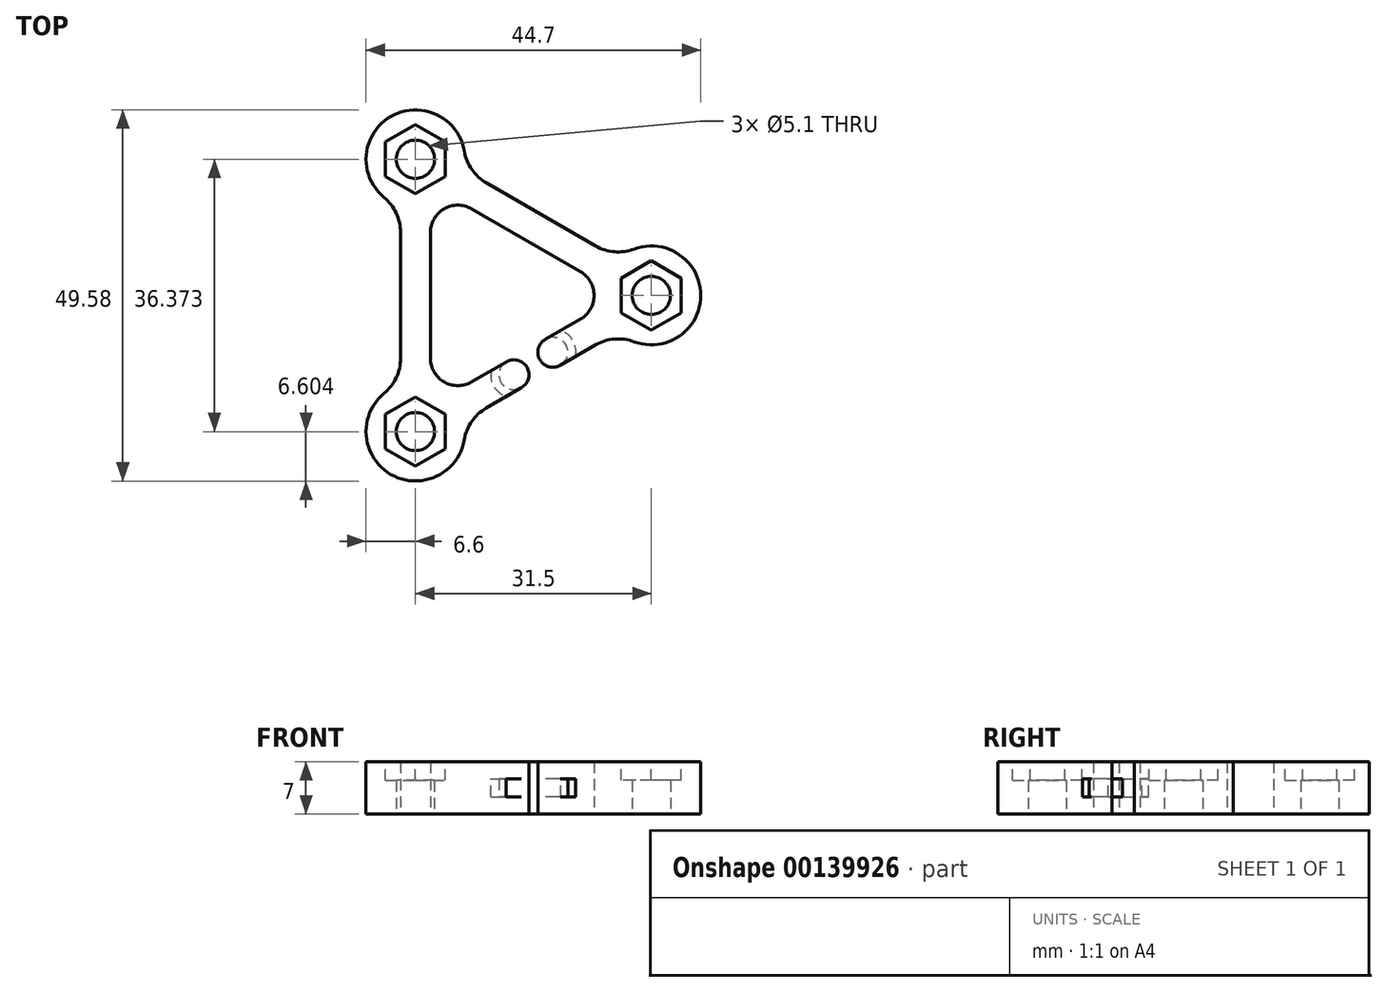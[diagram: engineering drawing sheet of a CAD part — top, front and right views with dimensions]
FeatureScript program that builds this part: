
annotation { "Feature Type Name" : "Feature", "Feature Type Description" : "" }
export const myFeature = defineFeature(function(context is Context, id is Id, definition is map)
    precondition{}
    {
        {
            var Q0;
            Q0=qCreatedBy(makeId("Top.planeOp"),FACE);
            var sketch = newSketch(context, id + "F0", { "sketchPlane" : qUnion([Q0])});
            skCircle(sketch, "E0", {"center": v(-31.5, 18.19) * mm, "radius": 2.55 * mm});
            skCircle(sketch, "E1", {"center": v(-31.5, -18.19) * mm, "radius": 2.55 * mm});
            skCircle(sketch, "E2", {"center": v(0, 0) * mm, "radius": 2.55 * mm});
            skArc(sketch, "E3", {"start": v(-25, 19.3) * mm, "mid": v(-34.8, 23.9) * mm, "end": v(-35.7, 13.1) * mm});
            skArc(sketch, "E4", {"start": v(-35.7, -13.1) * mm, "mid": v(-34.8, -23.9) * mm, "end": v(-25, -19.3) * mm});
            skArc(sketch, "E5", {"start": v(-2.3, -6.19) * mm, "mid": v(6.6, 0) * mm, "end": v(-2.3, 6.19) * mm});
            skLineSegment(sketch, "E6", {"start": v(-24.03, 11.56) * mm, "end": v(-9.47, 3.16) * mm});
            skLineSegment(sketch, "E7", {"start": v(-22.03, 15.03) * mm, "end": v(-7.47, 6.62) * mm});
            skLineSegment(sketch, "E8", {"start": v(-31.5, 18.19) * mm, "end": v(0, 0) * mm, "construction": true});
            skLineSegment(sketch, "E9", {"start": v(0, 0) * mm, "end": v(-31.5, -18.19) * mm, "construction": true});
            skLineSegment(sketch, "E10", {"start": v(-31.5, -18.19) * mm, "end": v(-31.5, 18.19) * mm, "construction": true});
            skArc(sketch, "E11", {"start": v(-24.03, 11.56) * mm, "mid": v(-27.68, 11.56) * mm, "end": v(-29.5, 8.4) * mm});
            skArc(sketch, "E12", {"start": v(-29.5, -8.4) * mm, "mid": v(-27.68, -11.56) * mm, "end": v(-24.03, -11.56) * mm});
            skArc(sketch, "E13", {"start": v(-9.47, -3.16) * mm, "mid": v(-7.65, 0) * mm, "end": v(-9.47, 3.16) * mm});
            skArc(sketch, "E14", {"start": v(-35.7, -13.1) * mm, "mid": v(-34.08, -11) * mm, "end": v(-33.5, -8.4) * mm});
            skArc(sketch, "E15", {"start": v(-22.03, -15.03) * mm, "mid": v(-23.99, -16.83) * mm, "end": v(-25, -19.3) * mm});
            skArc(sketch, "E16", {"start": v(-33.5, 8.4) * mm, "mid": v(-34.08, 11) * mm, "end": v(-35.7, 13.1) * mm});
            skArc(sketch, "E17", {"start": v(-25, 19.3) * mm, "mid": v(-23.99, 16.83) * mm, "end": v(-22.03, 15.03) * mm});
            skArc(sketch, "E18", {"start": v(-7.47, 6.62) * mm, "mid": v(-4.93, 5.83) * mm, "end": v(-2.3, 6.19) * mm});
            skArc(sketch, "E19", {"start": v(-2.3, -6.19) * mm, "mid": v(-4.93, -5.83) * mm, "end": v(-7.47, -6.62) * mm});
            skLineSegment(sketch, "E20", {"start": v(-24.03, 11.56) * mm, "end": v(-22.03, 15.03) * mm, "construction": true});
            skLineSegment(sketch, "E21", {"start": v(-9.47, 3.16) * mm, "end": v(-7.47, 6.62) * mm, "construction": true});
            skLineSegment(sketch, "E22", {"start": v(-9.47, -3.16) * mm, "end": v(-7.47, -6.62) * mm, "construction": true});
            skLineSegment(sketch, "E23", {"start": v(-33.5, -8.4) * mm, "end": v(-29.5, -8.4) * mm, "construction": true});
            skLineSegment(sketch, "E24", {"start": v(-22.03, -15.03) * mm, "end": v(-24.03, -11.56) * mm, "construction": true});
            skLineSegment(sketch, "E25", {"start": v(-33.5, -8.4) * mm, "end": v(-33.5, 8.4) * mm});
            skLineSegment(sketch, "E26", {"start": v(-29.5, -8.4) * mm, "end": v(-29.5, 8.4) * mm});
            skLineSegment(sketch, "E27", {"start": v(-33.5, 8.4) * mm, "end": v(-29.5, 8.4) * mm, "construction": true});
            skLineSegment(sketch, "E28", {"start": v(-24.03, -11.56) * mm, "end": v(-19.35, -8.86) * mm});
            skLineSegment(sketch, "E29", {"start": v(-14.15, -5.86) * mm, "end": v(-9.47, -3.16) * mm});
            skLineSegment(sketch, "E30", {"start": v(-22.03, -15.03) * mm, "end": v(-17.35, -12.33) * mm});
            skLineSegment(sketch, "E31", {"start": v(-7.47, -6.62) * mm, "end": v(-12.15, -9.33) * mm});
            skArc(sketch, "E32", {"start": v(-17.35, -12.33) * mm, "mid": v(-16.62, -9.6) * mm, "end": v(-19.35, -8.86) * mm});
            skArc(sketch, "E33", {"start": v(-14.15, -5.86) * mm, "mid": v(-14.88, -8.6) * mm, "end": v(-12.15, -9.33) * mm});
            skSolve(sketch);
        }
        {
            var Q0;
            Q0=makeQuery(id+"F0.imprint","IMPRINT",FACE,{"disambiguationData":[TD([[makeQuery(id+"F0.imprint","IMPRINT",EDGE,{"derivedFrom":sQuery(id+"F0.wireOp",EDGE,"E0")}),-1.0]])]});
            extrude(context, id + "F1", {"entities" : qUnion([Q0]), "depth" : 7 * mm});
        }
        {
            var Q0;
            Q0=makeQuery(id+"F1.opExtrude","CAP_FACE",FACE,{"disambiguationData":[OSD([sQuery(id+"F0.wireOp",EDGE,"E0"),sQuery(id+"F0.wireOp",EDGE,"E1"),sQuery(id+"F0.wireOp",EDGE,"E2"),sQuery(id+"F0.wireOp",EDGE,"E3"),sQuery(id+"F0.wireOp",EDGE,"E4"),sQuery(id+"F0.wireOp",EDGE,"E5"),sQuery(id+"F0.wireOp",EDGE,"T5Vw66OG-G5OR-DHDx-KvU7-dnTMRq0o1A0g"),sQuery(id+"F0.wireOp",EDGE,"8mzCXc7P-Lu7A-tcA2-hDls-zUZMRrlwUirj"),sQuery(id+"F0.wireOp",EDGE,"n4Ubmgs8-MzYA-ilAs-um63-DOsCIZ42xYd5"),sQuery(id+"F0.wireOp",EDGE,"iCspHw3C-Pdpp-QPBW-yDHl-MGOv44Ga2VXa"),sQuery(id+"F0.wireOp",EDGE,"xnWTmErK-ZSIG-ryMW-Ekzr-RR3PqCajZfuL"),sQuery(id+"F0.wireOp",EDGE,"AKW5OVUo-PFRE-jSi0-v7oE-Iw4JobIG5vWv"),sQuery(id+"F0.wireOp",EDGE,"E6"),sQuery(id+"F0.wireOp",EDGE,"JkiSf5jC-OJZR-1wmq-AVkU-QwjWYPwXVpW3"),sQuery(id+"F0.wireOp",EDGE,"9YlTFYq7-sXvY-dmJ4-6YRE-gBgDyT6P94yA")])],"isStart":false});
            var sketch = newSketch(context, id + "F2", { "sketchPlane" : qUnion([Q0])});
            skCircle(sketch, "E34.cCircle", {"center": v(-31.5, 18.19) * mm, "radius": 4 * mm, "construction": true});
            skLineSegment(sketch, "E34.0", {"start": v(-27.5, 20.5) * mm, "end": v(-27.5, 15.88) * mm});
            skLineSegment(sketch, "E34.1", {"start": v(-27.5, 15.88) * mm, "end": v(-31.5, 13.57) * mm});
            skLineSegment(sketch, "E34.2", {"start": v(-31.5, 13.57) * mm, "end": v(-35.5, 15.88) * mm});
            skLineSegment(sketch, "E34.3", {"start": v(-35.5, 15.88) * mm, "end": v(-35.5, 20.5) * mm});
            skLineSegment(sketch, "E34.4", {"start": v(-35.5, 20.5) * mm, "end": v(-31.5, 22.8) * mm});
            skLineSegment(sketch, "E34.5", {"start": v(-31.5, 22.8) * mm, "end": v(-27.5, 20.5) * mm});
            skPoint(sketch, "E34.0.midPoint", {"position": v(-27.5, 18.19) * mm});
            skCircle(sketch, "E35.cCircle", {"center": v(-31.5, -18.19) * mm, "radius": 4 * mm, "construction": true});
            skLineSegment(sketch, "E35.0", {"start": v(-27.5, -15.88) * mm, "end": v(-27.5, -20.5) * mm});
            skLineSegment(sketch, "E35.1", {"start": v(-27.5, -20.5) * mm, "end": v(-31.5, -22.8) * mm});
            skLineSegment(sketch, "E35.2", {"start": v(-31.5, -22.8) * mm, "end": v(-35.5, -20.5) * mm});
            skLineSegment(sketch, "E35.3", {"start": v(-35.5, -20.5) * mm, "end": v(-35.5, -15.88) * mm});
            skLineSegment(sketch, "E35.4", {"start": v(-35.5, -15.88) * mm, "end": v(-31.5, -13.57) * mm});
            skLineSegment(sketch, "E35.5", {"start": v(-31.5, -13.57) * mm, "end": v(-27.5, -15.88) * mm});
            skPoint(sketch, "E35.0.midPoint", {"position": v(-27.5, -18.19) * mm});
            skCircle(sketch, "E36.cCircle", {"center": v(0, 0) * mm, "radius": 4 * mm, "construction": true});
            skLineSegment(sketch, "E36.0", {"start": v(-4, -2.3) * mm, "end": v(-4, 2.3) * mm});
            skLineSegment(sketch, "E36.1", {"start": v(-4, 2.3) * mm, "end": v(0, 4.62) * mm});
            skLineSegment(sketch, "E36.2", {"start": v(0, 4.62) * mm, "end": v(4, 2.3) * mm});
            skLineSegment(sketch, "E36.3", {"start": v(4, 2.3) * mm, "end": v(4, -2.3) * mm});
            skLineSegment(sketch, "E36.4", {"start": v(4, -2.3) * mm, "end": v(0, -4.62) * mm});
            skLineSegment(sketch, "E36.5", {"start": v(0, -4.62) * mm, "end": v(-4, -2.3) * mm});
            skPoint(sketch, "E36.0.midPoint", {"position": v(-4, 0) * mm});
            skLineSegment(sketch, "E37", {"start": v(-31.5, -18.19) * mm, "end": v(-21, 0) * mm, "construction": true});
            skLineSegment(sketch, "E38", {"start": v(-21, 0) * mm, "end": v(-31.5, 18.19) * mm, "construction": true});
            skLineSegment(sketch, "E39", {"start": v(-21, 0) * mm, "end": v(0, 0) * mm, "construction": true});
            skLineSegment(sketch, "E40", {"start": v(-29, 0) * mm, "end": v(-17, 6.93) * mm, "construction": true});
            skPoint(sketch, "E40.startSnap0", {"position": v(-10.5, 0) * mm});
            skLineSegment(sketch, "E41", {"start": v(-17, 6.93) * mm, "end": v(-17, -6.93) * mm, "construction": true});
            skLineSegment(sketch, "E42", {"start": v(-17, -6.93) * mm, "end": v(-29, 0) * mm, "construction": true});
            skPoint(sketch, "E43", {"position": v(-23, 3.46) * mm});
            skPoint(sketch, "E44", {"position": v(-23, -3.46) * mm});
            skPoint(sketch, "E45", {"position": v(-17, 0) * mm});
            skSolve(sketch);
        }
        {
            var Q0;
            Q0=qSketchRegion(id+"F2",true);
            extrude(context, id + "F3", {"entities" : qUnion([Q0]), "operationType" : NewBodyOperationType.REMOVE, "oppositeDirection" : true, "depth" : 2.5 * mm});
        }
        {
            var Q0;
            Q0=qCreatedBy(makeId("Top.planeOp"),FACE);
            var Q1;
            Q1=makeQuery(id+"F2.imprint","IMPRINT",FACE,{"disambiguationData":[TD([[makeQuery(id+"F2.imprint","IMPRINT",EDGE,{"derivedFrom":sQuery(id+"F2.wireOp",EDGE,"E34.0")}),1.0]])]});
            cPlane(context, id + "F4", {"entities" : qUnion([Q0, Q1]), "cplaneType" : CPlaneType.MID_PLANE, "offset" : 3 * mm, "oppositeDirection" : true, "width" : 150 * mm, "height" : 150 * mm});
        }
        {
            var Q0;
            Q0=qCreatedBy(id+"F4.planeOp",FACE);
            var sketch = newSketch(context, id + "F5", { "sketchPlane" : qUnion([Q0])});
            skLineSegment(sketch, "E46", {"start": v(-17.35, -12.33) * mm, "end": v(-17.35, -12.33) * mm});
            skLineSegment(sketch, "E47", {"start": v(-19.35, -8.86) * mm, "end": v(-19.35, -8.86) * mm});
            skLineSegment(sketch, "E48", {"start": v(-12.15, -9.33) * mm, "end": v(-12.15, -9.33) * mm});
            skLineSegment(sketch, "E49", {"start": v(-14.15, -5.86) * mm, "end": v(-14.15, -5.86) * mm});
            skArc(sketch, "E50", {"start": v(-21.4, -10.05) * mm, "mid": v(-21.03, -12.14) * mm, "end": v(-19.4, -13.5) * mm});
            skArc(sketch, "E51", {"start": v(-12.15, -9.33) * mm, "mid": v(-11.42, -6.6) * mm, "end": v(-14.15, -5.86) * mm});
            skArc(sketch, "E52", {"start": v(-19.35, -8.86) * mm, "mid": v(-20.08, -11.6) * mm, "end": v(-17.35, -12.33) * mm});
            skLineSegment(sketch, "E53", {"start": v(-21.4, -10.05) * mm, "end": v(-19.35, -8.86) * mm});
            skLineSegment(sketch, "E54", {"start": v(-17.35, -12.33) * mm, "end": v(-19.4, -13.5) * mm});
            skArc(sketch, "E55", {"start": v(-10.1, -8.14) * mm, "mid": v(-10.47, -6.04) * mm, "end": v(-12.1, -4.68) * mm});
            skLineSegment(sketch, "E56", {"start": v(-12.1, -4.68) * mm, "end": v(-14.15, -5.86) * mm});
            skLineSegment(sketch, "E57", {"start": v(-12.15, -9.33) * mm, "end": v(-10.1, -8.14) * mm});
            skSolve(sketch);
        }
        {
            var Q0;
            Q0=qSketchRegion(id+"F5",true);
            extrude(context, id + "F6", {"entities" : qUnion([Q0]), "operationType" : NewBodyOperationType.REMOVE, "oppositeDirection" : true, "depth" : 2.4 * mm, "symmetric" : true});
        }
    });
